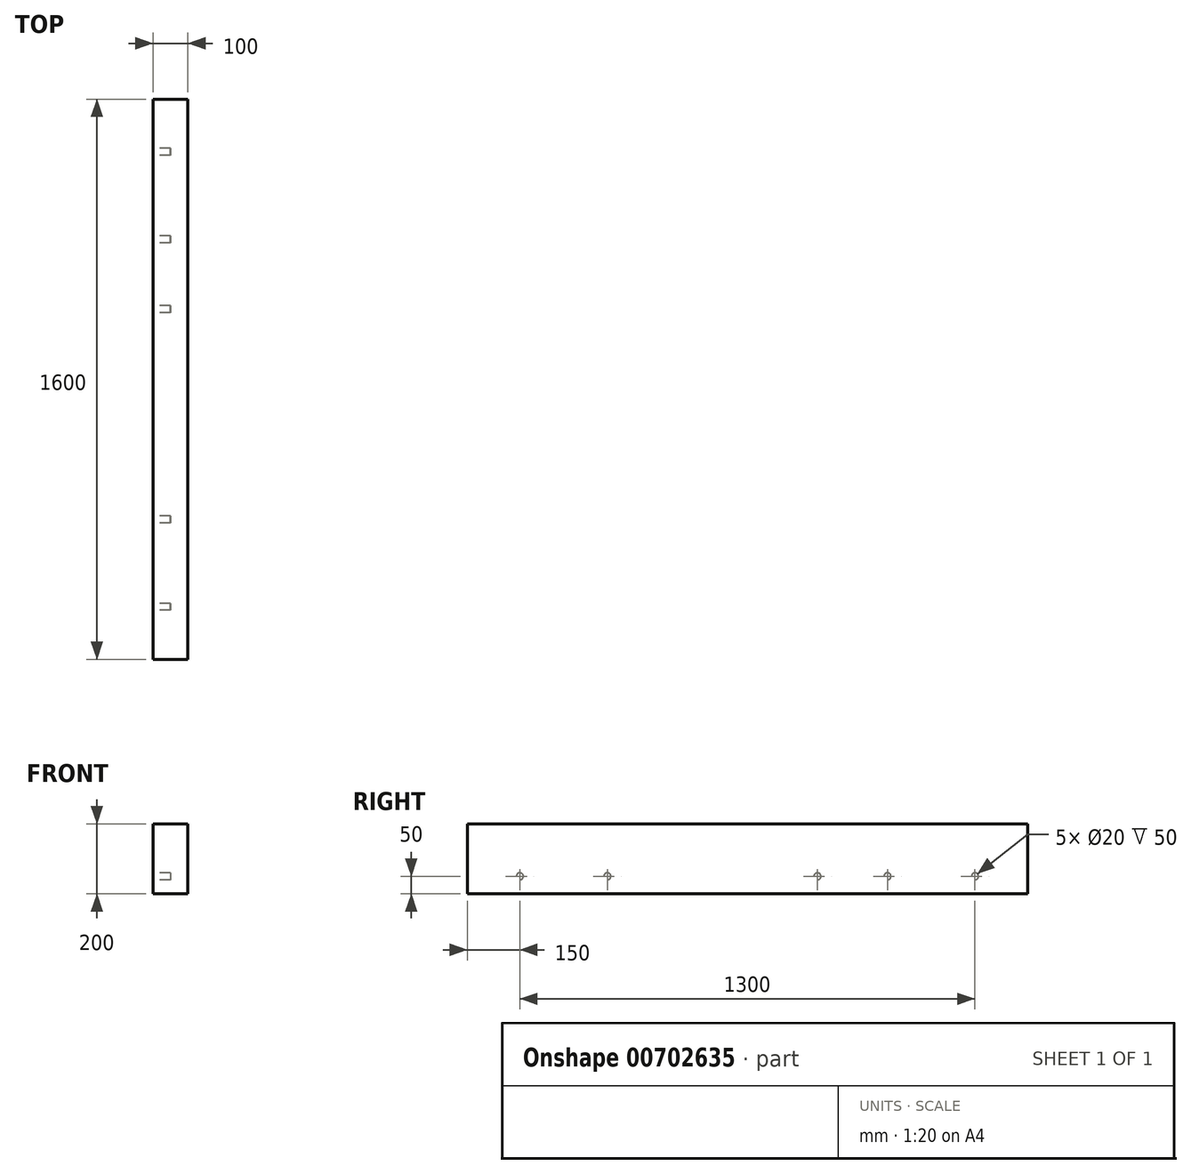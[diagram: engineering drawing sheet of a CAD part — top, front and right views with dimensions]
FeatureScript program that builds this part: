
annotation { "Feature Type Name" : "Feature", "Feature Type Description" : "" }
export const myFeature = defineFeature(function(context is Context, id is Id, definition is map)
    precondition{}
    {
        {
            var Q0;
            Q0=qCreatedBy(makeId("Front.planeOp"),FACE);
            var sketch = newSketch(context, id + "F0", { "sketchPlane" : qUnion([Q0])});
            skLineSegment(sketch, "E0.bottom", {"start": v(0, 0) * mm, "end": v(-100, 0) * mm});
            skLineSegment(sketch, "E0.top", {"start": v(0, 200) * mm, "end": v(-100, 200) * mm});
            skLineSegment(sketch, "E0.left", {"start": v(0, 0) * mm, "end": v(0, 200) * mm});
            skLineSegment(sketch, "E0.right", {"start": v(-100, 0) * mm, "end": v(-100, 200) * mm});
            skSolve(sketch);
        }
        {
            var Q0;
            Q0 = qSketchRegion(id + "F0", true);
            extrude(context, id + "F1", {"entities" : qUnion([Q0]), "depth" : 1600 * mm, "offsetDistance" : 25 * mm});
        }
        {
            var Q0;
            Q0=makeQuery(id+"F1.opExtrude","SWEPT_FACE",FACE,{"disambiguationData":[OSD([sQuery(id+"F0.wireOp",EDGE,"E0.right")])]});
            var sketch = newSketch(context, id + "F2", { "sketchPlane" : qUnion([Q0])});
            skLineSegment(sketch, "E1", {"start": v(-202.9, 50) * mm, "end": v(1820.2, 50) * mm, "construction": true});
            skCircle(sketch, "E2", {"center": v(150, 50) * mm, "radius": 10 * mm});
            skCircle(sketch, "E3", {"center": v(400, 50) * mm, "radius": 10 * mm});
            skCircle(sketch, "E4", {"center": v(600, 50) * mm, "radius": 10 * mm});
            skCircle(sketch, "E5", {"center": v(1200, 50) * mm, "radius": 10 * mm});
            skCircle(sketch, "E6", {"center": v(1450, 50) * mm, "radius": 10 * mm});
            skSolve(sketch);
        }
        {
            var Q0;
            Q0 = qSketchRegion(id + "F2", true);
            extrude(context, id + "F3", {"entities" : qUnion([Q0]), "operationType" : NewBodyOperationType.REMOVE, "oppositeDirection" : true, "depth" : 50 * mm, "offsetDistance" : 25 * mm});
        }
    });
